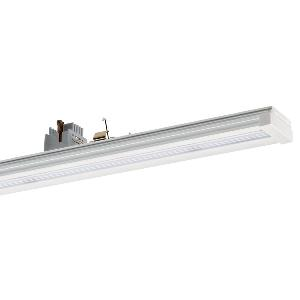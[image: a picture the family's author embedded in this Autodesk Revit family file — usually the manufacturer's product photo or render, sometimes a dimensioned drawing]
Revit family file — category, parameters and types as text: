
# Revit family: conveo_-_cvg_4500_850_xn-p_ea_5_226848209-00804958_1daf
name_source: partatom
category: Lighting Fixtures
units: mm (PartAtom-declared; Revit-internal decimal feet)

## family parameters
Cut with Voids When Loaded = No
Host = Face
Light Source = No
Part Type = Normal
Room Calculation Point = No
Round Connector Dimension = Use Diameter
Shared = No

## types (1)
- CONVEO - CVG 4500/850/xN-P/EA/5 (1 x LED, 4300 lm, 5000K)
    Apparent Load = 28 VA
    Approval mark = CE
    CIE Flux Codes = 57 84 97 100 100
    Color Rendering = 80-89
    Color Temperature = 5000K
    Control Gear = Electronic ballast
    Default Elevation = 1800 mm
    Description = CVG 4500/850/xN-P/EA/5|Continuous-row system|light source: LED|work equipment: Electronic ballast|connected load: 220-240 V, 50-60 Hz|Power consumption: approx. 28 W|luminous flux: 4300 lm|luminous efficacy: 153 lm/W|colour temperature: Cold white, ca. 5000 K|color rendering index (CRI): >= 80|chromaticity tolerance:  3 SDCM|System of protection: IP 54|class of protection: I|technology: Switchable|luminaire body|material: Aluminium|surface: Powder coatet|colour: White|lamp cover: Acrylic (PMMA), Satine|weight (net): approx. 1.9 kg|Fastening: Available separately|minimum ambient temperature: -25 ░C|maximum ambient temperature: 56 ░C|glare control: Prism optics (linear)|Approval mark: VDE - ENEC|
    Frequency = 50 Hz
    Height = 70 mm
    Lamp = 1 x LED
    Lamp Light Flux = 4300 lm
    Lamp count = 1
    Length = 1500 mm
    Luminous efficacy = 154 lm/W
    Manufacturer = Waldmann
    ModVariant = No
    Model = 226848209-00804958
    Mounting Place = Ceiling
    Mounting Type = Pendant
    Number of Poles = 1
    OnlyDefault = Yes
    Power Factor = 1
    Product Name = CONVEO - CVG 4500/850/xN-P/EA/5
    Product group = Continuous-row system (industry)
    ProductGroupID = 301
    Protection Class = Protection class I
    Protection Degree = IP 54
    RLX_Detail_Level = 1
    RlxData = <blob elided: 99629 chars, md5=ee436366>
    Socket = socket
    Standby Power = 0 W
    System Light Flux = 4300 lm
    System Power = 28 W
    Type Comments = Product without accessories
    Type Image = 226848079-00804943-1p5.jpg
    URL = http://relux.com
    VarID = ---
    Voltage = 230 V
    Voltage Range = 220-240 V
    Weight = 0.00 kg
    Width = 64 mm

## geometry (parser evidence)
native form markers: Blend x4, Sweep x10
no freeform markers — native parametric forms only
